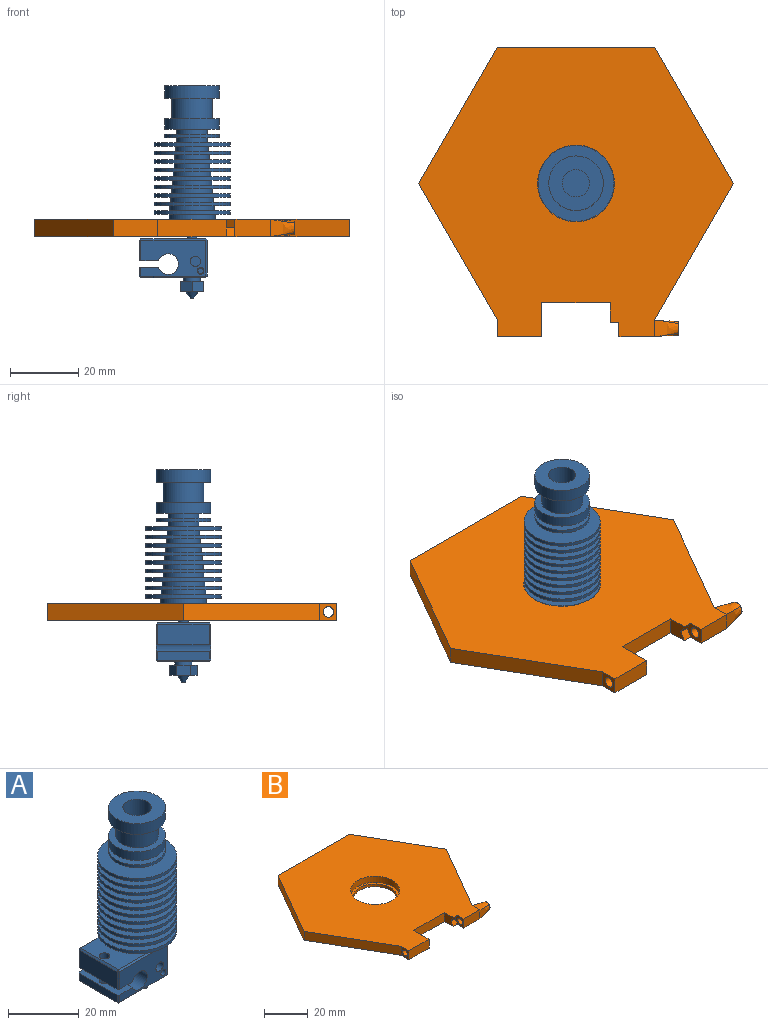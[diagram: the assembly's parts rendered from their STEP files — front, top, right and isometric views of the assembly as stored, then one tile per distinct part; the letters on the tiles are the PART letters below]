
ASSEMBLY  parts=2 mates=1
PART A: 111 faces, bbox 26.7x22.3x62.3 mm
  f0: plane 0.5x0.5mm, normal (-0.58,0.58,0.58), area 0.2mm2, adj f18,f20,f21
  f1: plane 0.5x0.5mm, normal (0.58,0.58,0.58), area 0.2mm2, adj f4,f17,f20
  f2: plane 0.5x0.5mm, normal (-0.58,-0.58,0.58), area 0.2mm2, adj f6,f18,f19
  f3: plane 0.5x0.5mm, normal (0.58,0.58,-0.58), area 0.2mm2, adj f4,f9,f16
  f4: plane 10.5x0.5mm, normal (0.71,0.71,0), area 7.4mm2, adj f1,f3,f27,f51
  f5: plane 0.5x0.5mm, normal (0.58,-0.58,0.58), area 0.2mm2, adj f6,f11,f17
  f6: plane 19x0.5mm, normal (0,-0.71,0.71), area 13.4mm2, adj f2,f5,f22,f25
  f7: plane 0.5x0.5mm, normal (-0.58,0.58,-0.58), area 0.2mm2, adj f8,f9,f14
  f8: plane 2.5x0.5mm, normal (-0.71,0.71,0), area 1.8mm2, adj f7,f50,f51,f52
  f9: plane 19x0.5mm, normal (0,0.71,-0.71), area 13.4mm2, adj f3,f7,f26,f51
  f10: plane 0.5x0.5mm, normal (0.58,-0.58,-0.58), area 0.2mm2, adj f11,f15,f16
  f11: plane 10.5x0.5mm, normal (0.71,-0.71,0), area 7.4mm2, adj f5,f10,f22,f27
  f12: plane 0.5x0.5mm, normal (-0.58,-0.58,-0.58), area 0.2mm2, adj f13,f14,f15
  f13: plane 2.5x0.5mm, normal (-0.71,-0.71,0), area 1.8mm2, adj f12,f22,f50,f52
  f14: plane 15x0.5mm, normal (-0.71,0,-0.71), area 10.6mm2, adj f7,f12,f26,f52
  f15: plane 19x0.5mm, normal (0,-0.71,-0.71), area 13.4mm2, adj f10,f12,f22,f26
  f16: plane 15x0.5mm, normal (0.71,0,-0.71), area 10.6mm2, adj f3,f10,f26,f27
  f17: plane 15x0.5mm, normal (0.71,0,0.71), area 10.6mm2, adj f1,f5,f25,f27
  f18: plane 15x0.5mm, normal (-0.71,0,0.71), area 10.6mm2, adj f0,f2,f23,f25
  f19: plane 6x0.5mm, normal (-0.71,-0.71,0), area 4.2mm2, adj f2,f22,f23,f24
  f20: plane 19x0.5mm, normal (0,0.71,0.71), area 13.4mm2, adj f0,f1,f25,f51
  f21: plane 6x0.5mm, normal (-0.71,0.71,0), area 4.2mm2, adj f0,f23,f24,f51
  f22: plane 19x10.5mm, normal (0,-1,0), area 150.5mm2, adj f6,f11,f13,f15,f19,f24,f43,f47
  f23: plane 15x6mm, normal (-1,0,0), area 90mm2, adj f18,f19,f21,f24
  f24: plane 16x5.65mm, normal (0,0,-1), area 83mm2, adj f19,f21,f22,f23,f42,f49,f51
  f25: plane 19x15mm, normal (0,0,1), area 271.8mm2, adj f6,f17,f18,f20,f42,f53
  f26: plane 19x15mm, normal (0,0,-1), area 258.3mm2, adj f9,f14,f15,f16,f40,f41
  f27: plane 15x10.5mm, normal (1,0,0), area 157.5mm2, adj f4,f11,f16,f17
  f28: cylinder r=0.2mm len=3mm, axis (0,0,1), area 3.8mm2, adj f29,f30
  f29: plane 0.4x0.4mm, normal (0,0,-1), area 0.1mm2, adj f28
  f30: plane 1x1mm, normal (0,0,-1), area 0.7mm2, adj f28,f31
  f31: cone r=1.9mm half-angle=35deg, axis (0,0,1), area 18.4mm2, adj f30,f39
  f32: plane 8.08x7mm, normal (0,0,1), area 22.8mm2, adj f33,f34,f35,f36,f37,f38,f40
  f33: plane 3.5x3mm, normal (-0.5,-0.87,0), area 12.1mm2, adj f32,f34,f38,f39
  f34: plane 3.5x3mm, normal (0.5,-0.87,0), area 12.1mm2, adj f32,f33,f35,f39
  f35: plane 4.04x3mm, normal (1,0,0), area 12.1mm2, adj f32,f34,f36,f39
  f36: plane 3.5x3mm, normal (0.5,0.87,0), area 12.1mm2, adj f32,f35,f37,f39
  f37: plane 3.5x3mm, normal (-0.5,0.87,0), area 12.1mm2, adj f32,f36,f38,f39
  f38: plane 4.04x3mm, normal (-1,0,0), area 12.1mm2, adj f32,f33,f37,f39
  f39: plane 8.08x7mm, normal (0,0,-1), area 31.1mm2, adj f31,f33,f34,f35,f36,f37,f38
  f40: cylinder r=2.5mm len=5mm, axis (0,0,-1), area 15.7mm2, adj f26,f32
  f41: cylinder r=1.5mm len=3mm, axis (0,0,-1), area 28.3mm2, adj f26,f50
  f42: cylinder r=1.5mm len=6.5mm, axis (0,0,-1), area 61.3mm2, adj f24,f25
  f43: cylinder r=1mm len=2mm, axis (0,1,0), area 12.6mm2, adj f22,f44
  f44: plane 2x2mm, normal (0,-1,0), area 1.3mm2, adj f43,f45
  f45: cylinder r=0.78mm len=2.45mm, axis (0,1,0), area 11.9mm2, adj f44,f46
  f46: plane 1.55x1.55mm, normal (0,-1,0), area 1.9mm2, adj f45
  f47: cylinder r=1.5mm len=3.45mm, axis (0,1,0), area 32.5mm2, adj f22,f48
  f48: plane 3x3mm, normal (0,-1,0), area 7.1mm2, adj f47
  f49: cylinder r=3.02mm len=16mm, axis (0,1,0), area 271.5mm2, adj f22,f24,f50,f51
  f50: plane 16x5.65mm, normal (0,0,1), area 83mm2, adj f8,f13,f22,f41,f49,f51,f52
  f51: plane 19x10.5mm, normal (0,1,0), area 160.7mm2, adj f4,f8,f9,f20,f21,f24,f49,f50
  f52: plane 15x2.5mm, normal (-1,0,0), area 37.5mm2, adj f8,f13,f14,f50
  f53: cylinder r=1.4mm len=2.8mm, axis (0,0,-1), area 18.5mm2, adj f25,f110
  f54: cylinder r=4mm len=8mm, axis (0,0,-1), area 163.4mm2, adj f55,f56
  f55: plane 8x8mm, normal (0,0,1), area 50.3mm2, adj f54
  f56: plane 16x16mm, normal (0,0,1), area 150.8mm2, adj f54,f57
  f57: cylinder r=8mm len=16mm, axis (0,0,-1), area 186mm2, adj f56,f58
  f58: plane 16x16mm, normal (0,0,-1), area 88mm2, adj f57,f59
  f59: cylinder r=6mm len=12mm, axis (0,0,-1), area 226.2mm2, adj f58,f60
  f60: plane 16x16mm, normal (0,0,1), area 88mm2, adj f59,f61
  f61: cylinder r=8mm len=16mm, axis (0,0,-1), area 150.8mm2, adj f60,f62
  f62: plane 16x16mm, normal (0,0,-1), area 137.4mm2, adj f61,f63
  f63: cylinder r=4.5mm len=9mm, axis (0,0,-1), area 42.4mm2, adj f62,f64
  f64: plane 16x16mm, normal (0,0,1), area 137.4mm2, adj f63,f65
  f65: cylinder r=8mm len=16mm, axis (0,0,-1), area 50.3mm2, adj f64,f66
  f66: plane 16x16mm, normal (0,0,-1), area 137.4mm2, adj f65,f67
  f67: cylinder r=4.5mm len=9mm, axis (0,0,-1), area 42.4mm2, adj f66,f68
  f68: plane 22.3x22.3mm, normal (0,0,1), area 327mm2, adj f67,f69
  f69: cylinder r=11.15mm len=22.3mm, axis (0,0,-1), area 70.1mm2, adj f68,f70
  f70: plane 22.3x22.3mm, normal (0,0,-1), area 319.7mm2, adj f69,f71
  f71: cylinder r=4.75mm len=9.5mm, axis (0,0,-1), area 44.8mm2, adj f70,f72
  f72: plane 22.3x22.3mm, normal (0,0,1), area 319.7mm2, adj f71,f73
  f73: cylinder r=11.15mm len=22.3mm, axis (0,0,-1), area 70.1mm2, adj f72,f74
  f74: plane 22.3x22.3mm, normal (0,0,-1), area 312mm2, adj f73,f75
  f75: cylinder r=5mm len=10mm, axis (0,0,-1), area 47.1mm2, adj f74,f76
  f76: plane 22.3x22.3mm, normal (0,0,1), area 312mm2, adj f75,f77
  f77: cylinder r=11.15mm len=22.3mm, axis (0,0,-1), area 70.1mm2, adj f76,f78
  f78: plane 22.3x22.3mm, normal (0,0,-1), area 304mm2, adj f77,f79
  f79: cylinder r=5.25mm len=10.5mm, axis (0,0,-1), area 49.5mm2, adj f78,f80
  f80: plane 22.3x22.3mm, normal (0,0,1), area 304mm2, adj f79,f81
  f81: cylinder r=11.15mm len=22.3mm, axis (0,0,-1), area 70.1mm2, adj f80,f82
  f82: plane 22.3x22.3mm, normal (0,0,-1), area 295.5mm2, adj f81,f83
  f83: cylinder r=5.5mm len=11mm, axis (0,0,-1), area 51.8mm2, adj f82,f84
  f84: plane 22.3x22.3mm, normal (0,0,1), area 295.5mm2, adj f83,f85
  f85: cylinder r=11.15mm len=22.3mm, axis (0,0,-1), area 70.1mm2, adj f84,f86
  f86: plane 22.3x22.3mm, normal (0,0,-1), area 286.7mm2, adj f85,f87
  f87: cylinder r=5.75mm len=11.5mm, axis (0,0,-1), area 54.2mm2, adj f86,f88
  f88: plane 22.3x22.3mm, normal (0,0,1), area 286.7mm2, adj f87,f89
  f89: cylinder r=11.15mm len=22.3mm, axis (0,0,-1), area 70.1mm2, adj f88,f90
  f90: plane 22.3x22.3mm, normal (0,0,-1), area 277.5mm2, adj f89,f91
  f91: cylinder r=6mm len=12mm, axis (0,0,-1), area 56.5mm2, adj f90,f92
  f92: plane 22.3x22.3mm, normal (0,0,1), area 277.5mm2, adj f91,f93
  f93: cylinder r=11.15mm len=22.3mm, axis (0,0,-1), area 70.1mm2, adj f92,f94
  f94: plane 22.3x22.3mm, normal (0,0,-1), area 267.9mm2, adj f93,f95
  f95: cylinder r=6.25mm len=12.5mm, axis (0,0,-1), area 58.9mm2, adj f94,f96
  f96: plane 22.3x22.3mm, normal (0,0,1), area 267.9mm2, adj f95,f97
  f97: cylinder r=11.15mm len=22.3mm, axis (0,0,-1), area 70.1mm2, adj f96,f98
  f98: plane 22.3x22.3mm, normal (0,0,-1), area 257.8mm2, adj f97,f99
  f99: cylinder r=6.5mm len=13mm, axis (0,0,-1), area 61.3mm2, adj f98,f100
  f100: plane 22.3x22.3mm, normal (0,0,1), area 257.8mm2, adj f99,f101
  f101: cylinder r=11.15mm len=22.3mm, axis (0,0,-1), area 70.1mm2, adj f100,f102
  f102: plane 22.3x22.3mm, normal (0,0,-1), area 247.4mm2, adj f101,f103
  f103: cylinder r=6.75mm len=13.5mm, axis (0,0,-1), area 63.6mm2, adj f102,f104
  f104: plane 22.3x22.3mm, normal (0,0,1), area 247.4mm2, adj f103,f105
  f105: cylinder r=11.15mm len=22.3mm, axis (0,0,-1), area 70.1mm2, adj f104,f106
  f106: plane 22.3x22.3mm, normal (0,0,-1), area 236.6mm2, adj f105,f107
  f107: cylinder r=7mm len=14mm, axis (0,0,-1), area 66mm2, adj f106,f108
  f108: plane 22.3x22.3mm, normal (0,0,1), area 236.6mm2, adj f107,f109
  f109: cylinder r=11.15mm len=22.3mm, axis (0,0,-1), area 70.1mm2, adj f108,f110
  f110: plane 22.3x22.3mm, normal (0,0,-1), area 384.4mm2, adj f53,f109
PART B: 26 faces, bbox 92.4x85x5 mm
  f0: plane 5.71x5mm, normal (-1,0,0), area 24.9mm2, adj f2,f3,f15,f21,f23
  f1: plane 10.49x5mm, normal (0,-1,0), area 52.5mm2, adj f2,f3,f20,f22
  f2: plane 92.38x85mm, normal (0,0,1), area 5164.7mm2, adj f0,f1,f4,f5,f6,f7,f8,f9
  f3: plane 92.38x85mm, normal (0,0,-1), area 5248.2mm2, adj f0,f1,f4,f5,f6,f7,f8,f11
  f4: plane 40x23.09mm, normal (0.87,-0.5,0), area 230.9mm2, adj f2,f3,f5,f18
  f5: plane 40x23.09mm, normal (0.87,0.5,0), area 230.9mm2, adj f2,f3,f4,f6
  f6: plane 46.19x5mm, normal (0,1,0), area 230.9mm2, adj f2,f3,f5,f7
  f7: plane 40x23.09mm, normal (-0.87,0.5,0), area 230.9mm2, adj f2,f3,f6,f8
  f8: plane 40x23.09mm, normal (-0.87,-0.5,0), area 230.9mm2, adj f2,f3,f7,f12
  f9: cylinder r=11.25mm len=22.5mm, axis (0,0,1), area 247.4mm2, adj f2,f10
  f10: plane 22.5x22.5mm, normal (0,0,1), area 83.4mm2, adj f9,f11
  f11: cylinder r=10mm len=20mm, axis (0,0,1), area 94.2mm2, adj f3,f10
  f12: plane 5x5mm, normal (-1,0,0), area 17.5mm2, adj f2,f3,f8,f13,f25
  f13: plane 13.09x5mm, normal (0,-1,0), area 65.5mm2, adj f2,f3,f12,f14
  f14: plane 10x5mm, normal (1,0,0), area 42.5mm2, adj f2,f3,f13,f15,f25
  f15: plane 20x5mm, normal (0,-1,0), area 100mm2, adj f0,f2,f3,f14
  f16: plane 4x4mm, normal (1,0,0), area 5mm2, adj f17,f18,f19,f20,f24
  f17: bspline ~7x5mm, area 28.2mm2, adj f3,f16,f18,f20
  f18: bspline ~7x5mm, area 28.2mm2, adj f4,f16,f17,f19
  f19: bspline ~7x5mm, area 28.2mm2, adj f2,f16,f18,f20
  f20: bspline ~7x5mm, area 28.2mm2, adj f1,f16,f17,f19
  f21: plane 2.6x2.5mm, normal (0,-0.87,0.5), area 7.5mm2, adj f0,f3,f22,f23
  f22: plane 5.73x5mm, normal (-1,0,0), area 17.5mm2, adj f1,f2,f3,f21,f23,f24
  f23: plane 2.6x2.5mm, normal (0,-0.87,-0.5), area 7.5mm2, adj f0,f2,f21,f22
  f24: cylinder r=1.55mm len=17.49mm, axis (1,0,0), area 170.4mm2, adj f16,f22
  f25: cylinder r=1.55mm len=13.09mm, axis (1,0,0), area 127.5mm2, adj f12,f14
PLACE A t=(0,0,40.95)mm
PLACE B t=(0,0,18.1)mm
MATE fastened A.f53 <-> B.f11  axis (0,0,-1) through (0,0,19.6)mm
